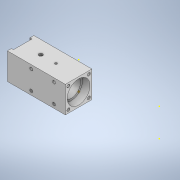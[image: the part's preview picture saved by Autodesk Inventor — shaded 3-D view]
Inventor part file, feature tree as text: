
AUTODESK INVENTOR PART (.ipt)
format: ipt  version: 2022 (Build 260153000, 153)  size: 273,920 bytes
history: native  units: mm
features: sketch x9, plane x4, extrude x4, hole x3, chamfer x3, projected_geometry x2, other x1, revolve x1, mirror x1
ambient origin geometry x8: Origin, YZ Plane, XZ Plane, XY Plane, X Axis, Y Axis, Z Axis, Center Point
bodies: Body1 (feature_tree)
feature tree (28):
  sketch  "Sketch1"  dims[d0=76.5mm d1=35.0mm]
  sketch  "Sketch3"  dims[d2=30.0mm d3=25.5mm]
  plane  "Work Plane1"
  sketch  "Sketch4"  dims[d4=10.0mm d5=25.0mm]
  other  "Work Point1"
  sketch  "Sketch5"  dims[d6=30.0mm d10=35.0mm]
  plane  "Work Plane2"
  extrude  "Extrusion1"  Depth=35.0mm
  revolve  "Revolution2"  [1 undecoded]
  hole  "Hole1"  [1 undecoded]
  sketch  "Sketch8"  dims[d14=90.0deg d21=38.18mm]
  extrude  "Extrusion2"  Depth=35.0mm
  hole  "Hole2"  [1 undecoded]
  plane  "Work Plane3"
  sketch  "Sketch9"  dims[d22=3.0mm d23=40.0mm d25=360.0deg]
  sketch  "Sketch11"  dims[d27=2.5mm d28=6.0mm d29=3.0mm d30=5.0mm d31=90.0deg d32=7.0mm d33=20.594885mm d34=2.5mm]
  extrude  "Extrusion3"  Depth=38.18mm
  extrude  "Extrusion4"  Depth=40.0mm TaperAngle=360.0deg
  hole  "Hole3"  [1 undecoded]
  plane  "Work Plane4"
  mirror  "Mirror2"
  chamfer  "Chamfer3"  Distance=5.0mm
  chamfer  "Chamfer4"  Distance=1.0mm
  chamfer  "Chamfer5"  Distance=29.5mm
  sketch  "Sketch7"  dims[d11=35.0mm d12=10.0mm d13=0.0mm]
  projected_geometry  "Projected Loop1"
  sketch  "Sketch12"  dims[d35=2.5mm d36=5.0mm d38=1.0mm d39=29.5mm d40=24.4mm d41=2.75mm d42=0.0mm d43=2.0mm d44=6.0mm d45=2.5mm d46=4.0mm d47=90.0deg d48=5.0mm d49=20.594885mm d54=3.0mm d55=5.0mm d56=30.0mm d57=50.0mm d58=2.75mm d59=0.0mm d60=10.0mm d61=0.0mm d62=3.0mm d63=15.0mm d64=5.0mm d65=20.0mm d67=30.0mm d68=10.0mm d70=10.0mm d72=2.5mm d73=6.0mm d74=3.0mm d75=5.0mm d76=90.0deg d77=7.0mm d78=20.594885mm d85=0.5mm d86=2.0mm d87=45.0deg d88=0.5mm d89=2.0mm d90=45.0deg d91=0.5mm d92=2.0mm d93=45.0deg]
  projected_geometry  "Projected Loop2"
note: 4 required parameter values undecoded (feature->parameter linkage not recoverable at this tier; creation-order binding heuristic only, values carry confidence <= 0.55)